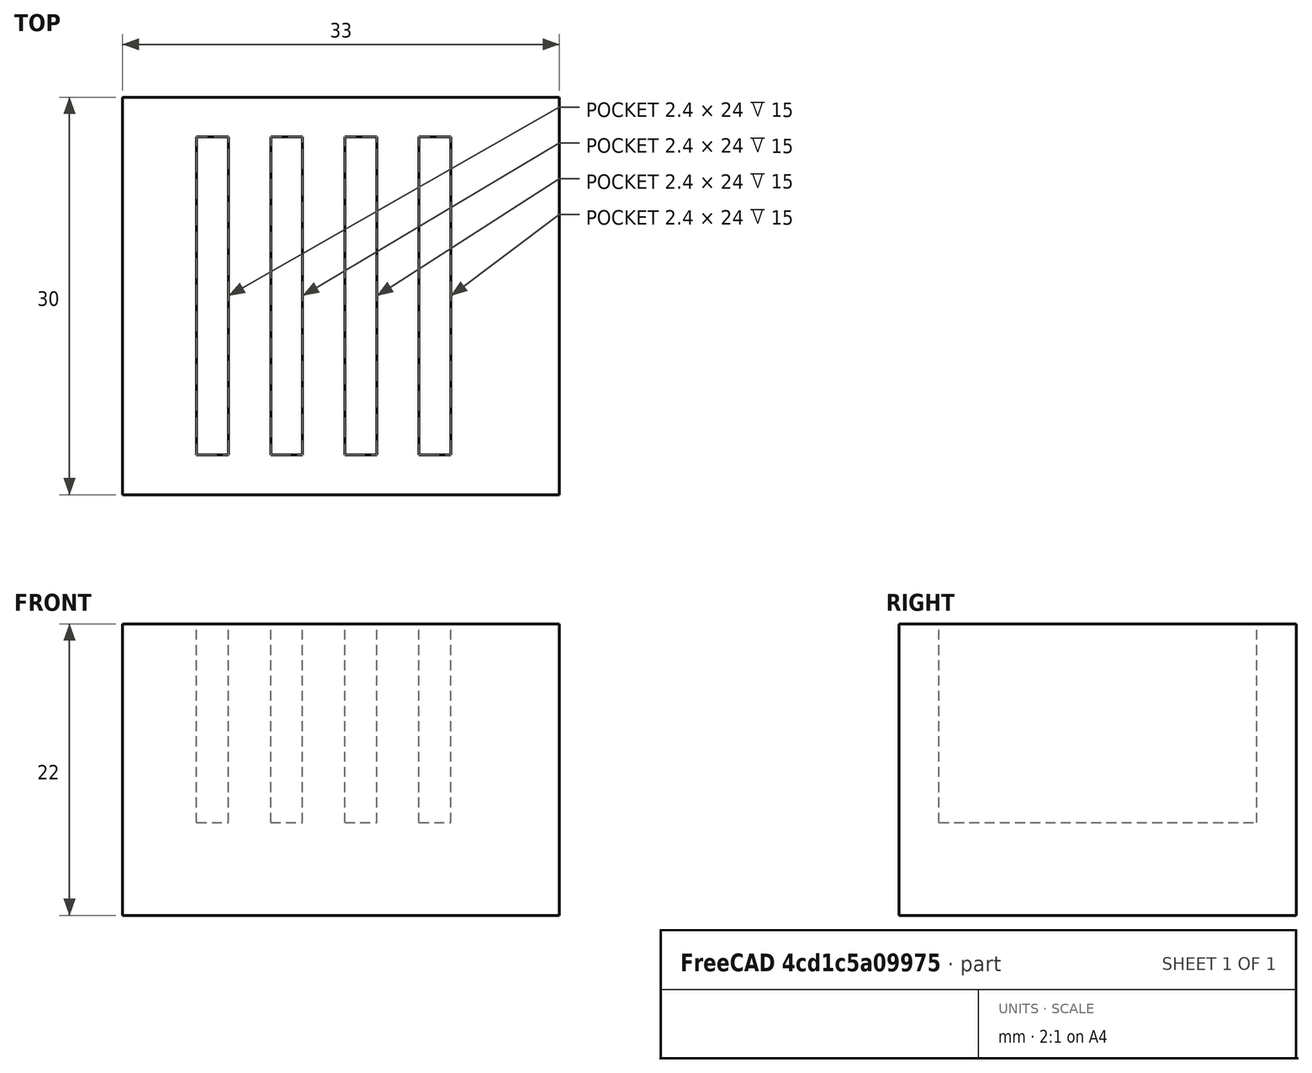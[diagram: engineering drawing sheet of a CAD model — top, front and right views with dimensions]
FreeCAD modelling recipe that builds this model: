
FCSTD DOCUMENT  (FreeCAD 0.20R29177 (Git))
Label: EjercicioVideo8
License: All rights reserved
LicenseURL: http://en.wikipedia.org/wiki/All_rights_reserved
objects: Part::Box×5, Part::MultiFuse×2, Part::Fuse×1, Part::Cut×1
note: 9 computed .brp shape members not serialized (recipe doc carries the construction recipe); baked Part::Feature solids carry a one-line shape summary decoded from their .brp

FEATURE [Part::Box] Box  label="Cubo_base"
  AttacherType = Attacher::AttachEngine3D
  Height = 22
  Length = 33
  Width = 30
FEATURE [Part::Box] Box001  label="ranura"
  AttacherType = Attacher::AttachEngine3D
  Height = 15
  Length = 2.4
  Placement = pos=(5.6,3,7) rot=(0,0,1;0rad)
  Width = 24
FEATURE [Part::Box] Box002  label="ranura001"
  AttacherType = Attacher::AttachEngine3D
  Height = 15
  Length = 2.4
  Placement = pos=(11.2,3,7) rot=(0,0,1;0rad)
  Width = 24
FEATURE [Part::Box] Box003  label="ranura002"
  AttacherType = Attacher::AttachEngine3D
  Height = 15
  Length = 2.4
  Placement = pos=(16.8,3,7) rot=(0,0,1;0rad)
  Width = 24
FEATURE [Part::Box] Box004  label="ranura003"
  AttacherType = Attacher::AttachEngine3D
  Height = 15
  Length = 2.4
  Placement = pos=(22.4,3,7) rot=(0,0,1;0rad)
  Width = 24
FEATURE [Part::Fuse] Fusion
  Base = -> Box003
  Tool = -> Box004
FEATURE [Part::MultiFuse] Fusion001
  Shapes = -> [Box002,Box001]
FEATURE [Part::MultiFuse] Fusion002
  Shapes = -> [Fusion001,Fusion]
FEATURE [Part::Cut] Cut
  Base = -> Box
  Tool = -> Fusion002
